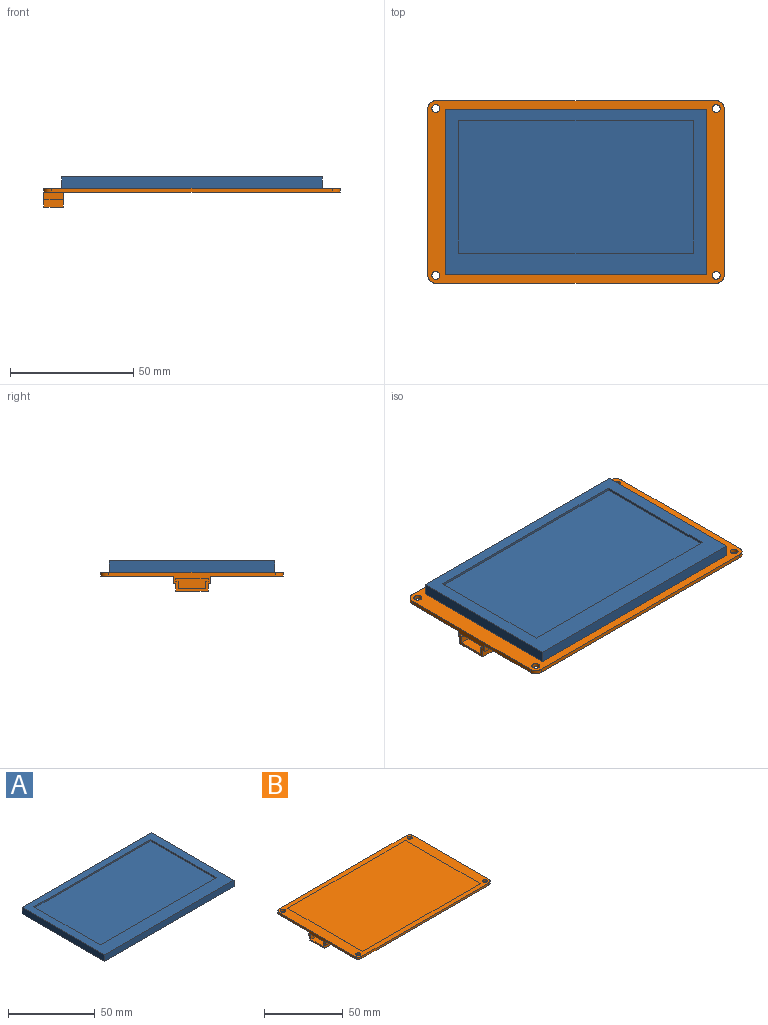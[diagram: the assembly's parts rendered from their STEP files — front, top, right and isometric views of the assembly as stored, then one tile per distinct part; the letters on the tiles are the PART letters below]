
ASSEMBLY  parts=2 mates=1
PART A: 11 faces, bbox 105.5x67.2x4.6 mm
  f0: plane 105.5x67.2mm, normal (0,0,1), area 1970.7mm2, adj f1,f2,f3,f4,f6,f7,f8,f9
  f1: plane 105.5x4.6mm, normal (0,1,0), area 485.3mm2, adj f0,f2,f4,f5
  f2: plane 67.2x4.6mm, normal (-1,0,0), area 309.1mm2, adj f0,f1,f3,f5
  f3: plane 105.5x4.6mm, normal (0,-1,0), area 485.3mm2, adj f0,f2,f4,f5
  f4: plane 67.2x4.6mm, normal (1,0,0), area 309.1mm2, adj f0,f1,f3,f5
  f5: plane 105.5x67.2mm, normal (0,0,-1), area 7089.6mm2, adj f1,f2,f3,f4
  f6: plane 95.04x1mm, normal (0,-1,0), area 95mm2, adj f0,f7,f9,f10
  f7: plane 53.86x1mm, normal (1,0,0), area 53.9mm2, adj f0,f6,f8,f10
  f8: plane 95.04x1mm, normal (0,1,0), area 95mm2, adj f0,f7,f9,f10
  f9: plane 53.86x1mm, normal (-1,0,0), area 53.9mm2, adj f0,f6,f8,f10
  f10: plane 95.04x53.86mm, normal (0,0,1), area 5118.9mm2, adj f6,f7,f8,f9
PART B: 36 faces, bbox 120x74x7.6 mm
  f0: plane 120x74mm, normal (0,0,-1), area 8721mm2, adj f2,f3,f4,f5,f6,f7,f8,f9
  f1: plane 120x74mm, normal (0,0,1), area 1749.4mm2, adj f2,f3,f4,f5,f6,f7,f8,f9
  f2: plane 113.6x1.6mm, normal (0,1,0), area 181.8mm2, adj f0,f1,f3,f12
  f3: cylinder r=3.2mm len=3.2mm, axis (0,0,-1), area 8mm2, adj f0,f1,f2,f4
  f4: plane 67.6x7.6mm, normal (-1,0,0), area 146.4mm2, adj f0,f1,f3,f5,f19,f20,f21,f22
  f5: cylinder r=3.2mm len=3.2mm, axis (0,0,-1), area 8mm2, adj f0,f1,f4,f6
  f6: plane 113.6x1.6mm, normal (0,-1,0), area 181.8mm2, adj f0,f1,f5,f7
  f7: cylinder r=3.2mm len=3.2mm, axis (0,0,-1), area 8mm2, adj f0,f1,f6,f8
  f8: plane 67.6x1.6mm, normal (1,0,0), area 108.2mm2, adj f0,f1,f7,f12
  f9: cylinder r=1.6mm len=3.2mm, axis (0,0,-1), area 16.1mm2, adj f0,f1
  f10: cylinder r=1.6mm len=3.2mm, axis (0,0,-1), area 16.1mm2, adj f0,f1
  f11: cylinder r=1.6mm len=3.2mm, axis (0,0,-1), area 16.1mm2, adj f0,f1
  f12: cylinder r=3.2mm len=3.2mm, axis (0,0,-1), area 8mm2, adj f0,f1,f2,f8
  f13: cylinder r=1.6mm len=3.2mm, axis (0,0,-1), area 16.1mm2, adj f0,f1
  f14: plane 105.5x0.01mm, normal (0,1,0), area 1.1mm2, adj f1,f15,f17,f18
  f15: plane 67.2x0.01mm, normal (-1,0,0), area 0.7mm2, adj f1,f14,f16,f18
  f16: plane 105.5x0.01mm, normal (0,-1,0), area 1.1mm2, adj f1,f15,f17,f18
  f17: plane 67.2x0.01mm, normal (1,0,0), area 0.7mm2, adj f1,f14,f16,f18
  f18: plane 105.5x67.2mm, normal (0,0,1), area 7089.6mm2, adj f14,f15,f16,f17
  f19: plane 7.81x3mm, normal (0,1,0), area 23.4mm2, adj f0,f4,f20,f26
  f20: plane 7.81x1mm, normal (0,0,-1), area 7.8mm2, adj f4,f19,f21,f26
  f21: plane 7.81x3mm, normal (0,1,0), area 23.4mm2, adj f4,f20,f22,f26
  f22: plane 13.12x7.81mm, normal (0,0,-1), area 102.5mm2, adj f4,f21,f23,f26
  f23: plane 7.81x3mm, normal (0,-1,0), area 23.4mm2, adj f4,f22,f24,f26
  f24: plane 7.81x1mm, normal (0,0,-1), area 7.8mm2, adj f4,f23,f25,f26
  f25: plane 7.81x3mm, normal (0,-1,0), area 23.4mm2, adj f0,f4,f24,f26
  f26: plane 15.12x6mm, normal (1,0,0), area 84.7mm2, adj f0,f19,f20,f21,f22,f23,f24,f25
  f27: plane 6x1mm, normal (0,1,0), area 6mm2, adj f4,f28,f34,f35
  f28: plane 13.12x6mm, normal (0,0,-1), area 78.7mm2, adj f4,f27,f29,f35
  f29: plane 6x1mm, normal (0,-1,0), area 6mm2, adj f4,f28,f30,f35
  f30: plane 6x1mm, normal (0,0,1), area 6mm2, adj f4,f29,f31,f35
  f31: plane 6x3mm, normal (0,-1,0), area 18mm2, adj f4,f30,f32,f35
  f32: plane 11.12x6mm, normal (0,0,1), area 66.7mm2, adj f4,f31,f33,f35
  f33: plane 6x3mm, normal (0,1,0), area 18mm2, adj f4,f32,f34,f35
  f34: plane 6x1mm, normal (0,0,1), area 6mm2, adj f4,f27,f33,f35
  f35: plane 13.12x4mm, normal (-1,0,0), area 46.5mm2, adj f27,f28,f29,f30,f31,f32,f33,f34
PLACE A t=(-15.56,-8.93,-34.32)mm
PLACE B t=(-15.56,-8.93,-34.33)mm
MATE fastened A.f5 <-> B.f18  axis (0,0,-1) through (-15.56,-8.93,-32.72)mm
